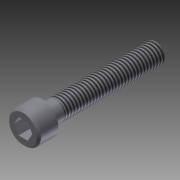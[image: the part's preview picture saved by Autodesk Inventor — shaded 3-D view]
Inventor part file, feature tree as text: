
AUTODESK INVENTOR PART (.ipt)
format: ipt  version: 2011 (Build 150239000, 239)  size: 102,912 bytes
history: native  units: in
note: dims shown in document units (in); Inventor stores cm internally (conversion verified against a paired STEP export)
features: extrude x3, sketch x3, chamfer x2, thread x1
ambient origin geometry x8: Origin, YZ Plane, XZ Plane, XY Plane, X Axis, Y Axis, Z Axis, Center Point
bodies: Solid1 (feature_tree)
feature tree (9):
  extrude  "Extrusion1"  Depth=0.19in TaperAngle=0.0deg
  extrude  "Extrusion2"  Depth=1.125in TaperAngle=0.0deg
  extrude  "Extrusion3"  Depth=0.125in TaperAngle=0.0deg
  thread  "Thread1"  [1 undecoded]
  chamfer  "Chamfer1"  Distance=0.02in Angle=45.0deg
  chamfer  "Chamfer2"  Distance=0.02in Angle=45.0deg
  sketch  "Sketch1"  dims[d0=0.312in d1=0.19in d2=0.0in]
  sketch  "Sketch2"  dims[d3=0.19in d4=1.125in d5=0.0in]
  sketch  "Sketch3"  dims[d6=0.1562in d7=0.125in d8=0.0in d9=1.0in d10=0.0in d11=0.02in d12=0.125in d13=45.0deg d14=0.02in d15=0.125in d16=45.0deg]
note: 1 required parameter value undecoded (feature->parameter linkage not recoverable at this tier; creation-order binding heuristic only, values carry confidence <= 0.55)
